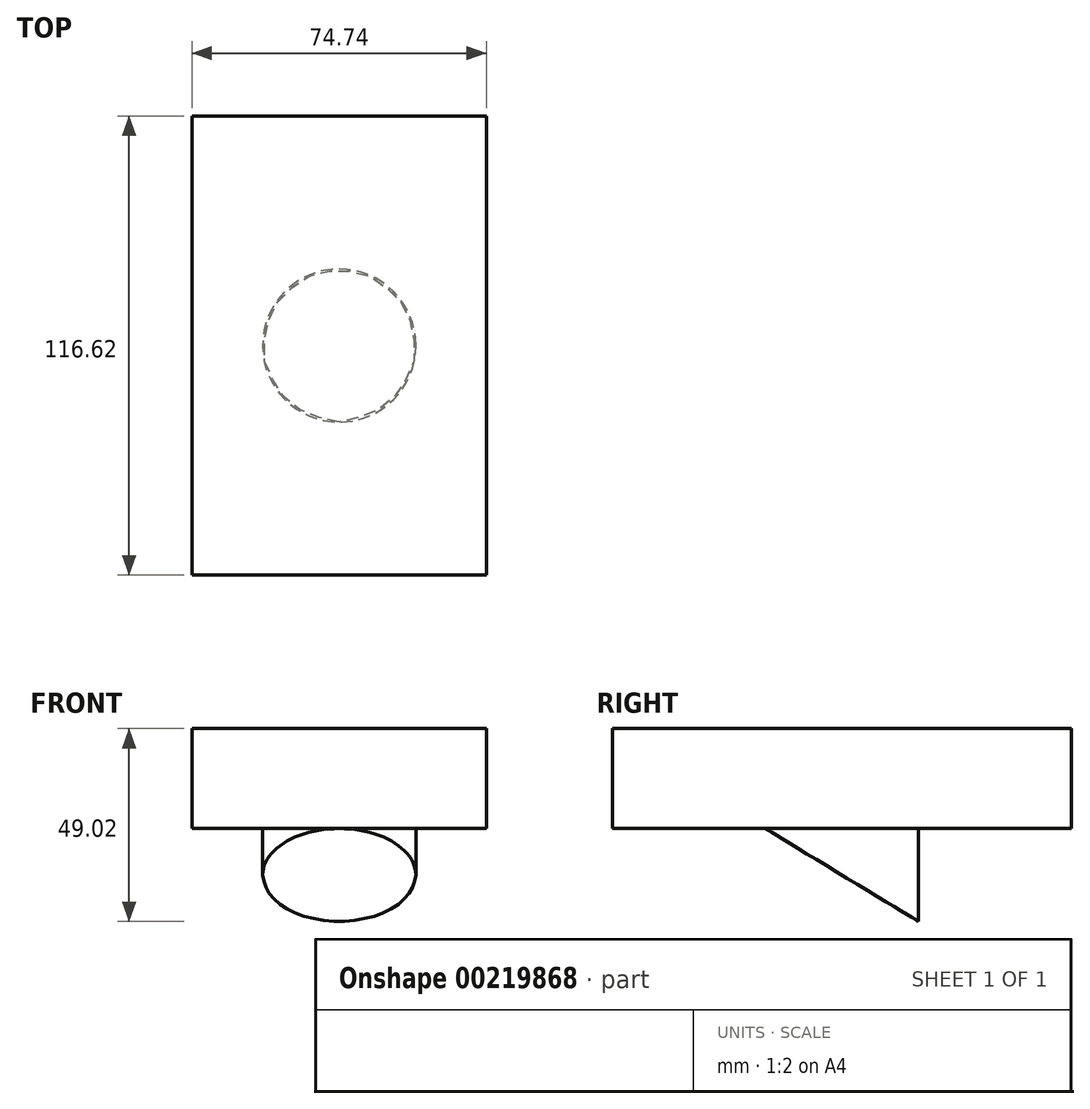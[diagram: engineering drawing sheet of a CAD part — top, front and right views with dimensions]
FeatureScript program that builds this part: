
annotation { "Feature Type Name" : "Feature", "Feature Type Description" : "" }
export const myFeature = defineFeature(function(context is Context, id is Id, definition is map)
    precondition{}
    {
        {
            var Q0;
            Q0=qCreatedBy(makeId("Top.planeOp"),FACE);
            var sketch = newSketch(context, id + "F0", { "sketchPlane" : qUnion([Q0])});
            skLineSegment(sketch, "E0.bottom", {"start": v(-37.37, 58.3) * mm, "end": v(37.37, 58.3) * mm});
            skLineSegment(sketch, "E0.top", {"start": v(-37.37, -58.3) * mm, "end": v(37.37, -58.3) * mm});
            skLineSegment(sketch, "E0.left", {"start": v(-37.37, 58.3) * mm, "end": v(-37.37, -58.3) * mm});
            skLineSegment(sketch, "E0.right", {"start": v(37.37, 58.3) * mm, "end": v(37.37, -58.3) * mm});
            skPoint(sketch, "E0.middle", {"position": v(0, 0) * mm});
            skCircle(sketch, "E1", {"center": v(0, 0) * mm, "radius": 19.45 * mm});
            skSolve(sketch);
        }
        {
            var Q0;
            Q0 = qSketchRegion(id + "F0", true);
            var Q1;
            Q1=makeQuery(id+"F0.imprint","IMPRINT",FACE,{"disambiguationData":[TD([[makeQuery(id+"F0.imprint","IMPRINT",EDGE,{"derivedFrom":sQuery(id+"F0.wireOp",EDGE,"E1")}),1.0]])]});
            extrude(context, id + "F1", {"entities" : qUnion([Q0, Q1]), "depth" : 25.4 * mm});
        }
        {
            var Q0;
            Q0=makeQuery(id+"F0.imprint","IMPRINT",FACE,{"disambiguationData":[TD([[makeQuery(id+"F0.imprint","IMPRINT",EDGE,{"derivedFrom":sQuery(id+"F0.wireOp",EDGE,"E1")}),1.0]])]});
            extrude(context, id + "F2", {"entities" : qUnion([Q0]), "operationType" : NewBodyOperationType.ADD, "oppositeDirection" : true, "depth" : 23.62 * mm});
        }
        {
            var Q0;
            Q0=makeQuery(id+"F1.opExtrude","SWEPT_FACE",FACE,{"disambiguationData":[OSD([sQuery(id+"F0.wireOp",EDGE,"E0.right")])]});
            var sketch = newSketch(context, id + "F3", { "sketchPlane" : qUnion([Q0])});
            skLineSegment(sketch, "E2.0", {"start": v(-19.45, -23.62) * mm, "end": v(19.45, -23.62) * mm});
            skLineSegment(sketch, "E3", {"start": v(-19.45, -23.62) * mm, "end": v(-19.45, 0) * mm});
            skLineSegment(sketch, "E4", {"start": v(-19.45, 0) * mm, "end": v(19.45, -23.62) * mm});
            skSolve(sketch);
        }
        {
            var Q0;
            Q0 = qSketchRegion(id + "F3", true);
            extrude(context, id + "F4", {"entities" : qUnion([Q0]), "operationType" : NewBodyOperationType.REMOVE, "endBound" : BoundingType.THROUGH_ALL, "oppositeDirection" : true, "depth" : 25.4 * mm});
        }
    });
